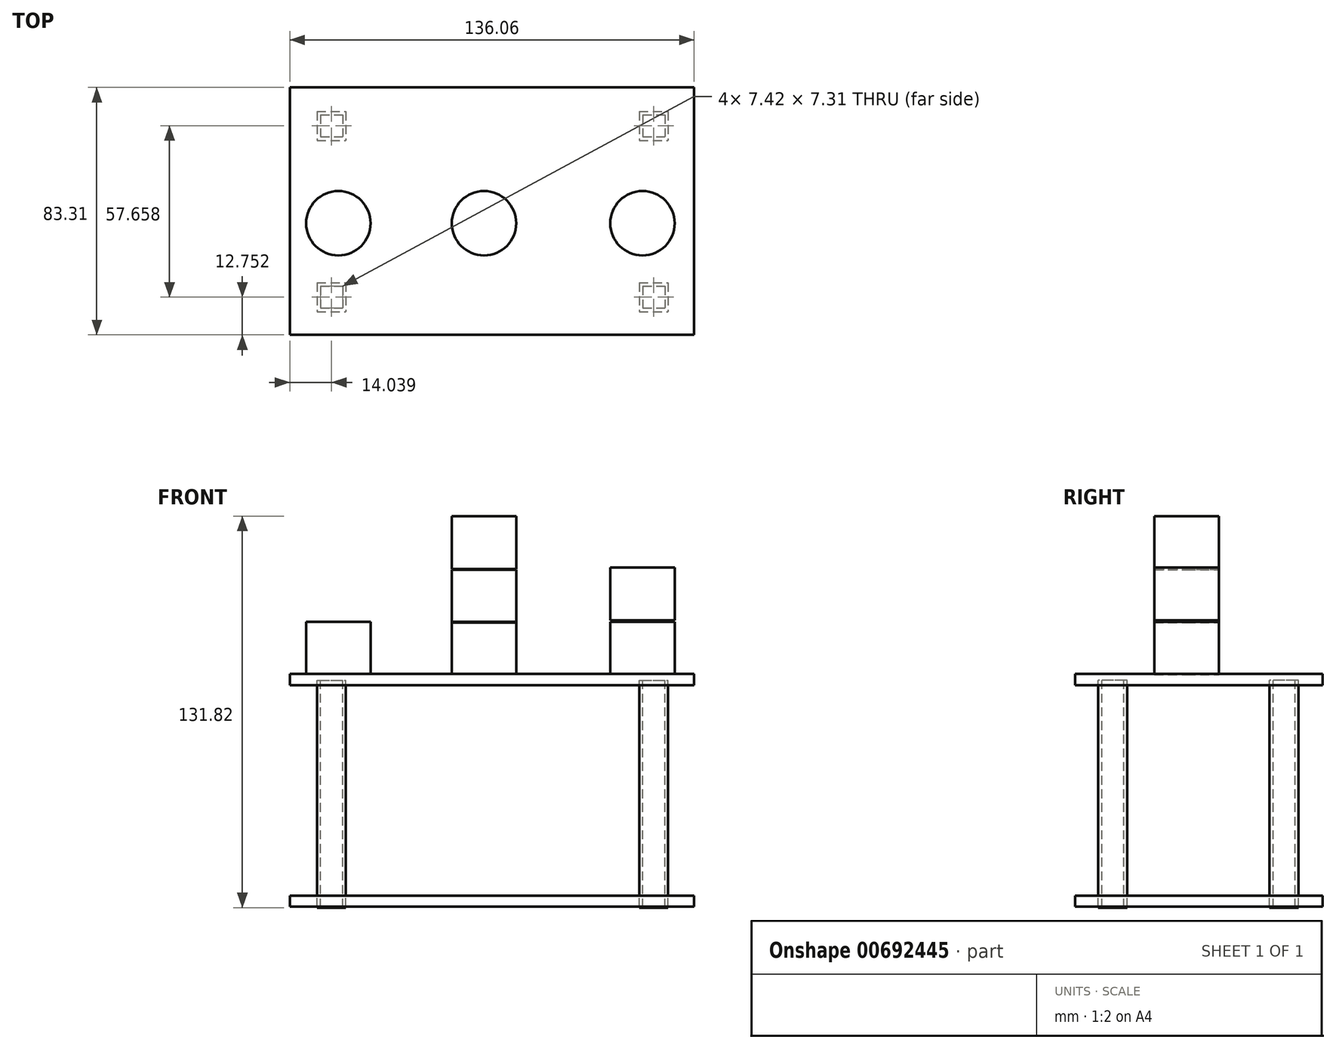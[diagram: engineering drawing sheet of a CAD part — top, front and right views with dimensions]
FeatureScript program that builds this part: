
annotation { "Feature Type Name" : "Feature", "Feature Type Description" : "" }
export const myFeature = defineFeature(function(context is Context, id is Id, definition is map)
    precondition{}
    {
        {
            var Q0;
            Q0=qCreatedBy(makeId("Front.planeOp"),FACE);
            var sketch = newSketch(context, id + "F0", { "sketchPlane" : qUnion([Q0])});
            skLineSegment(sketch, "E0", {"start": v(-67.33, -59.66) * mm, "end": v(68.73, -59.66) * mm});
            skLineSegment(sketch, "E1", {"start": v(68.73, -55.94) * mm, "end": v(-67.33, -55.94) * mm});
            skLineSegment(sketch, "E2", {"start": v(-67.33, -55.94) * mm, "end": v(-67.33, -59.66) * mm});
            skLineSegment(sketch, "E3", {"start": v(68.73, -55.94) * mm, "end": v(68.73, -59.66) * mm});
            skLineSegment(sketch, "E4", {"start": v(-67.33, 14.99) * mm, "end": v(68.73, 14.99) * mm});
            skLineSegment(sketch, "E5", {"start": v(68.73, 18.7) * mm, "end": v(-67.33, 18.7) * mm});
            skLineSegment(sketch, "E6", {"start": v(-67.33, 18.7) * mm, "end": v(-67.33, 14.99) * mm});
            skLineSegment(sketch, "E7", {"start": v(68.73, 18.7) * mm, "end": v(68.73, 14.99) * mm});
            skLineSegment(sketch, "E8", {"start": v(-56.17, 14.99) * mm, "end": v(-56.17, -55.94) * mm});
            skLineSegment(sketch, "E9", {"start": v(-52.45, 14.99) * mm, "end": v(-52.45, -55.94) * mm});
            skLineSegment(sketch, "E10", {"start": v(53.46, 15.34) * mm, "end": v(53.46, -55.58) * mm});
            skLineSegment(sketch, "E11", {"start": v(57.18, 15.34) * mm, "end": v(57.18, -55.58) * mm});
            skSolve(sketch);
        }
        {
            var Q0;
            Q0=makeQuery(id+"F0.imprint","IMPRINT",FACE,{"disambiguationData":[TD([[makeQuery(id+"F0.imprint","IMPRINT",EDGE,{"derivedFrom":sQuery(id+"F0.wireOp",EDGE,"E5")}),1.0]])]});
            var Q1;
            Q1=makeQuery(id+"F0.imprint","IMPRINT",FACE,{"disambiguationData":[TD([[makeQuery(id+"F0.imprint","IMPRINT",EDGE,{"derivedFrom":sQuery(id+"F0.wireOp",EDGE,"E0")}),1.0]])]});
            extrude(context, id + "F1", {"entities" : qUnion([Q0, Q1]), "depth" : 83.31 * mm, "offsetDistance" : 25.4 * mm});
        }
        {
            var Q0;
            Q0=makeQuery(id+"F1.opExtrude","SWEPT_FACE",FACE,{"disambiguationData":[OSD([sQuery(id+"F0.wireOp",EDGE,"E0")])]});
            var sketch = newSketch(context, id + "F2", { "sketchPlane" : qUnion([Q0])});
            skLineSegment(sketch, "E12.bottom", {"start": v(-58.2, 8.09) * mm, "end": v(-48.46, 8.09) * mm});
            skLineSegment(sketch, "E12.top", {"start": v(-58.2, 17.82) * mm, "end": v(-48.46, 17.82) * mm});
            skLineSegment(sketch, "E12.left", {"start": v(-58.2, 8.09) * mm, "end": v(-58.2, 17.82) * mm});
            skLineSegment(sketch, "E12.right", {"start": v(-48.46, 8.09) * mm, "end": v(-48.46, 17.82) * mm});
            skLineSegment(sketch, "E13.bottom", {"start": v(-57, 9.24) * mm, "end": v(-49.58, 9.24) * mm});
            skLineSegment(sketch, "E13.top", {"start": v(-57, 16.55) * mm, "end": v(-49.58, 16.55) * mm});
            skLineSegment(sketch, "E13.left", {"start": v(-57, 9.24) * mm, "end": v(-57, 16.55) * mm});
            skLineSegment(sketch, "E13.right", {"start": v(-49.58, 9.24) * mm, "end": v(-49.58, 16.55) * mm});
            skLineSegment(sketch, "E14.bottom", {"start": v(52.21, 8.09) * mm, "end": v(61.95, 8.09) * mm});
            skLineSegment(sketch, "E14.top", {"start": v(52.21, 17.82) * mm, "end": v(61.95, 17.82) * mm});
            skLineSegment(sketch, "E14.left", {"start": v(52.21, 8.09) * mm, "end": v(52.21, 17.82) * mm});
            skLineSegment(sketch, "E14.right", {"start": v(61.95, 8.09) * mm, "end": v(61.95, 17.82) * mm});
            skLineSegment(sketch, "E15.bottom", {"start": v(53.41, 9.24) * mm, "end": v(60.83, 9.24) * mm});
            skLineSegment(sketch, "E15.top", {"start": v(53.41, 16.55) * mm, "end": v(60.83, 16.55) * mm});
            skLineSegment(sketch, "E15.left", {"start": v(53.41, 9.24) * mm, "end": v(53.41, 16.55) * mm});
            skLineSegment(sketch, "E15.right", {"start": v(60.83, 9.24) * mm, "end": v(60.83, 16.55) * mm});
            skLineSegment(sketch, "E16.bottom", {"start": v(-58.2, 64.06) * mm, "end": v(-48.46, 64.06) * mm});
            skLineSegment(sketch, "E16.top", {"start": v(-58.2, 73.8) * mm, "end": v(-48.46, 73.8) * mm});
            skLineSegment(sketch, "E16.left", {"start": v(-58.2, 64.06) * mm, "end": v(-58.2, 73.8) * mm});
            skLineSegment(sketch, "E16.right", {"start": v(-48.46, 64.06) * mm, "end": v(-48.46, 73.8) * mm});
            skLineSegment(sketch, "E17.bottom", {"start": v(-57, 65.22) * mm, "end": v(-49.58, 65.22) * mm});
            skLineSegment(sketch, "E17.top", {"start": v(-57, 72.53) * mm, "end": v(-49.58, 72.53) * mm});
            skLineSegment(sketch, "E17.left", {"start": v(-57, 65.22) * mm, "end": v(-57, 72.53) * mm});
            skLineSegment(sketch, "E17.right", {"start": v(-49.58, 65.22) * mm, "end": v(-49.58, 72.53) * mm});
            skLineSegment(sketch, "E18.bottom", {"start": v(52.21, 64.06) * mm, "end": v(61.95, 64.06) * mm});
            skLineSegment(sketch, "E18.top", {"start": v(52.21, 73.8) * mm, "end": v(61.95, 73.8) * mm});
            skLineSegment(sketch, "E18.left", {"start": v(52.21, 64.06) * mm, "end": v(52.21, 73.8) * mm});
            skLineSegment(sketch, "E18.right", {"start": v(61.95, 64.06) * mm, "end": v(61.95, 73.8) * mm});
            skLineSegment(sketch, "E19.bottom", {"start": v(53.41, 65.22) * mm, "end": v(60.83, 65.22) * mm});
            skLineSegment(sketch, "E19.top", {"start": v(53.41, 72.53) * mm, "end": v(60.83, 72.53) * mm});
            skLineSegment(sketch, "E19.left", {"start": v(53.41, 65.22) * mm, "end": v(53.41, 72.53) * mm});
            skLineSegment(sketch, "E19.right", {"start": v(60.83, 65.22) * mm, "end": v(60.83, 72.53) * mm});
            skSolve(sketch);
        }
        {
            var Q0;
            Q0=makeQuery(id+"F2.imprint","IMPRINT",FACE,{"disambiguationData":[TD([[makeQuery(id+"F2.imprint","IMPRINT",EDGE,{"derivedFrom":sQuery(id+"F2.wireOp",EDGE,"E12.bottom")}),1.0]])]});
            extrude(context, id + "F3", {"entities" : qUnion([Q0]), "depth" : 0.28 * mm, "offsetDistance" : 25.4 * mm, "hasSecondDirection" : true, "secondDirectionOppositeDirection" : true, "secondDirectionDepth" : 76.2 * mm});
        }
        {
            var Q0;
            Q0=makeQuery(id+"F3.opExtrude","SWEPT_BODY",BODY,{"disambiguationData":[OSD([sQuery(id+"F2.wireOp",EDGE,"E12.bottom"),sQuery(id+"F2.wireOp",EDGE,"E12.top"),sQuery(id+"F2.wireOp",EDGE,"E12.left"),sQuery(id+"F2.wireOp",EDGE,"E12.right"),sQuery(id+"F2.wireOp",EDGE,"E13.bottom"),sQuery(id+"F2.wireOp",EDGE,"E13.top"),sQuery(id+"F2.wireOp",EDGE,"E13.left"),sQuery(id+"F2.wireOp",EDGE,"E13.right")])]});
            transform(context, id + "F4", {"entities" : qUnion([Q0]), "transformType" : TransformType.TRANSLATION_3D, "dx" : 108.46 * mm, "dy" : 0 * mm, "dz" : 0 * mm, "makeCopy" : true});
        }
        {
            var Q0;
            Q0=makeQuery(id+"F3.opExtrude","SWEPT_BODY",BODY,{"disambiguationData":[OSD([sQuery(id+"F2.wireOp",EDGE,"E12.bottom"),sQuery(id+"F2.wireOp",EDGE,"E12.top"),sQuery(id+"F2.wireOp",EDGE,"E12.left"),sQuery(id+"F2.wireOp",EDGE,"E12.right"),sQuery(id+"F2.wireOp",EDGE,"E13.bottom"),sQuery(id+"F2.wireOp",EDGE,"E13.top"),sQuery(id+"F2.wireOp",EDGE,"E13.left"),sQuery(id+"F2.wireOp",EDGE,"E13.right")])]});
            var Q1;
            Q1=makeQuery(id+"F4.opPattern","COPY",BODY,{"derivedFrom":makeQuery(id+"F3.opExtrude","SWEPT_BODY",BODY,{"disambiguationData":[OSD([sQuery(id+"F2.wireOp",EDGE,"E12.bottom"),sQuery(id+"F2.wireOp",EDGE,"E12.top"),sQuery(id+"F2.wireOp",EDGE,"E12.left"),sQuery(id+"F2.wireOp",EDGE,"E12.right"),sQuery(id+"F2.wireOp",EDGE,"E13.bottom"),sQuery(id+"F2.wireOp",EDGE,"E13.top"),sQuery(id+"F2.wireOp",EDGE,"E13.left"),sQuery(id+"F2.wireOp",EDGE,"E13.right")])]}),"instanceName":"1"});
            transform(context, id + "F5", {"entities" : qUnion([Q0, Q1]), "transformType" : TransformType.TRANSLATION_3D, "dx" : 0 * mm, "dy" : -57.66 * mm, "dz" : 0 * mm, "makeCopy" : true});
        }
        {
            var Q0;
            Q0=makeQuery(id+"F4.opPattern","COPY",BODY,{"derivedFrom":makeQuery(id+"F3.opExtrude","SWEPT_BODY",BODY,{"disambiguationData":[OSD([sQuery(id+"F2.wireOp",EDGE,"E12.bottom"),sQuery(id+"F2.wireOp",EDGE,"E12.top"),sQuery(id+"F2.wireOp",EDGE,"E12.left"),sQuery(id+"F2.wireOp",EDGE,"E12.right"),sQuery(id+"F2.wireOp",EDGE,"E13.bottom"),sQuery(id+"F2.wireOp",EDGE,"E13.top"),sQuery(id+"F2.wireOp",EDGE,"E13.left"),sQuery(id+"F2.wireOp",EDGE,"E13.right")])]}),"instanceName":"1"});
            var Q1;
            Q1=makeQuery(id+"F1.opExtrude","SWEPT_BODY",BODY,{"disambiguationData":[OSD([sQuery(id+"F0.wireOp",EDGE,"E0"),sQuery(id+"F0.wireOp",EDGE,"E1"),sQuery(id+"F0.wireOp",EDGE,"E2"),sQuery(id+"F0.wireOp",EDGE,"E3")])]});
            var Q2;
            Q2=makeQuery(id+"F1.opExtrude","SWEPT_BODY",BODY,{"disambiguationData":[OSD([sQuery(id+"F0.wireOp",EDGE,"E4"),sQuery(id+"F0.wireOp",EDGE,"E5"),sQuery(id+"F0.wireOp",EDGE,"E6"),sQuery(id+"F0.wireOp",EDGE,"E7")])]});
            var Q3;
            Q3=makeQuery(id+"F3.opExtrude","SWEPT_BODY",BODY,{"disambiguationData":[OSD([sQuery(id+"F2.wireOp",EDGE,"E12.bottom"),sQuery(id+"F2.wireOp",EDGE,"E12.top"),sQuery(id+"F2.wireOp",EDGE,"E12.left"),sQuery(id+"F2.wireOp",EDGE,"E12.right"),sQuery(id+"F2.wireOp",EDGE,"E13.bottom"),sQuery(id+"F2.wireOp",EDGE,"E13.top"),sQuery(id+"F2.wireOp",EDGE,"E13.left"),sQuery(id+"F2.wireOp",EDGE,"E13.right")])]});
            var Q4;
            Q4=makeQuery(id+"F5.opPattern","COPY",BODY,{"derivedFrom":makeQuery(id+"F3.opExtrude","SWEPT_BODY",BODY,{"disambiguationData":[OSD([sQuery(id+"F2.wireOp",EDGE,"E12.bottom"),sQuery(id+"F2.wireOp",EDGE,"E12.top"),sQuery(id+"F2.wireOp",EDGE,"E12.left"),sQuery(id+"F2.wireOp",EDGE,"E12.right"),sQuery(id+"F2.wireOp",EDGE,"E13.bottom"),sQuery(id+"F2.wireOp",EDGE,"E13.top"),sQuery(id+"F2.wireOp",EDGE,"E13.left"),sQuery(id+"F2.wireOp",EDGE,"E13.right")])]}),"instanceName":"1"});
            var Q5;
            Q5=makeQuery(id+"F5.opPattern","COPY",BODY,{"derivedFrom":makeQuery(id+"F4.opPattern","COPY",BODY,{"derivedFrom":makeQuery(id+"F3.opExtrude","SWEPT_BODY",BODY,{"disambiguationData":[OSD([sQuery(id+"F2.wireOp",EDGE,"E12.bottom"),sQuery(id+"F2.wireOp",EDGE,"E12.top"),sQuery(id+"F2.wireOp",EDGE,"E12.left"),sQuery(id+"F2.wireOp",EDGE,"E12.right"),sQuery(id+"F2.wireOp",EDGE,"E13.bottom"),sQuery(id+"F2.wireOp",EDGE,"E13.top"),sQuery(id+"F2.wireOp",EDGE,"E13.left"),sQuery(id+"F2.wireOp",EDGE,"E13.right")])]}),"instanceName":"1"}),"instanceName":"1"});
            transform(context, id + "F6", {"entities" : qUnion([Q0, Q1, Q2, Q3, Q4, Q5]), "transformType" : TransformType.TRANSLATION_3D, "dx" : 285.75 * mm, "dy" : 0 * mm, "dz" : 0 * mm, "makeCopy" : false});
        }
        {
            var Q0;
            Q0=qCreatedBy(makeId("Top.planeOp"),FACE);
            var sketch = newSketch(context, id + "F7", { "sketchPlane" : qUnion([Q0])});
            skCircle(sketch, "E20", {"center": v(-23.07, 19.55) * mm, "radius": 10.84 * mm});
            skSolve(sketch);
        }
        {
            var Q0;
            Q0=makeQuery(id+"F7.imprint","IMPRINT",FACE,{"disambiguationData":[TD([[makeQuery(id+"F7.imprint","IMPRINT",EDGE,{"derivedFrom":sQuery(id+"F7.wireOp",EDGE,"E20")}),1.0]])]});
            extrude(context, id + "F8", {"entities" : qUnion([Q0]), "depth" : 17.78 * mm, "offsetDistance" : 25.4 * mm});
        }
        {
            var Q0;
            Q0=makeQuery(id+"F8.opExtrude","SWEPT_BODY",BODY,{"disambiguationData":[OSD([sQuery(id+"F7.wireOp",EDGE,"E20")])]});
            transform(context, id + "F9", {"entities" : qUnion([Q0]), "transformType" : TransformType.TRANSLATION_3D, "dx" : 49.02 * mm, "dy" : 0 * mm, "dz" : 0 * mm, "makeCopy" : true});
        }
        {
            var Q0;
            Q0=makeQuery(id+"F8.opExtrude","SWEPT_BODY",BODY,{"disambiguationData":[OSD([sQuery(id+"F7.wireOp",EDGE,"E20")])]});
            var Q1;
            Q1=makeQuery(id+"F9.opPattern","COPY",BODY,{"derivedFrom":makeQuery(id+"F8.opExtrude","SWEPT_BODY",BODY,{"disambiguationData":[OSD([sQuery(id+"F7.wireOp",EDGE,"E20")])]}),"instanceName":"1"});
            transform(context, id + "F10", {"entities" : qUnion([Q0, Q1]), "transformType" : TransformType.TRANSLATION_3D, "dx" : -24.9 * mm, "dy" : 0 * mm, "dz" : 0 * mm, "makeCopy" : false});
        }
        {
            var Q0;
            Q0=makeQuery(id+"F8.opExtrude","SWEPT_BODY",BODY,{"disambiguationData":[OSD([sQuery(id+"F7.wireOp",EDGE,"E20")])]});
            transform(context, id + "F11", {"entities" : qUnion([Q0]), "transformType" : TransformType.TRANSLATION_3D, "dx" : 102.36 * mm, "dy" : 0 * mm, "dz" : 0 * mm, "makeCopy" : true});
        }
        {
            var Q0;
            Q0=makeQuery(id+"F9.opPattern","COPY",BODY,{"derivedFrom":makeQuery(id+"F8.opExtrude","SWEPT_BODY",BODY,{"disambiguationData":[OSD([sQuery(id+"F7.wireOp",EDGE,"E20")])]}),"instanceName":"1"});
            transform(context, id + "F12", {"entities" : qUnion([Q0]), "transformType" : TransformType.TRANSLATION_3D, "dx" : 0 * mm, "dy" : 0 * mm, "dz" : 17.53 * mm, "makeCopy" : true});
        }
        {
            var Q0;
            Q0=makeQuery(id+"F9.opPattern","COPY",BODY,{"derivedFrom":makeQuery(id+"F8.opExtrude","SWEPT_BODY",BODY,{"disambiguationData":[OSD([sQuery(id+"F7.wireOp",EDGE,"E20")])]}),"instanceName":"1"});
            transform(context, id + "F13", {"entities" : qUnion([Q0]), "transformType" : TransformType.TRANSLATION_3D, "dx" : 0 * mm, "dy" : 0 * mm, "dz" : 35.56 * mm, "makeCopy" : true});
        }
        {
            var Q0;
            Q0=makeQuery(id+"F11.opPattern","COPY",BODY,{"derivedFrom":makeQuery(id+"F8.opExtrude","SWEPT_BODY",BODY,{"disambiguationData":[OSD([sQuery(id+"F7.wireOp",EDGE,"E20")])]}),"instanceName":"1"});
            transform(context, id + "F14", {"entities" : qUnion([Q0]), "transformType" : TransformType.TRANSLATION_3D, "dx" : 0 * mm, "dy" : 0 * mm, "dz" : 18.29 * mm, "makeCopy" : true});
        }
        {
            var Q0;
            Q0=makeQuery(id+"F8.opExtrude","SWEPT_BODY",BODY,{"disambiguationData":[OSD([sQuery(id+"F7.wireOp",EDGE,"E20")])]});
            var Q1;
            Q1=makeQuery(id+"F9.opPattern","COPY",BODY,{"derivedFrom":makeQuery(id+"F8.opExtrude","SWEPT_BODY",BODY,{"disambiguationData":[OSD([sQuery(id+"F7.wireOp",EDGE,"E20")])]}),"instanceName":"1"});
            var Q2;
            Q2=makeQuery(id+"F11.opPattern","COPY",BODY,{"derivedFrom":makeQuery(id+"F8.opExtrude","SWEPT_BODY",BODY,{"disambiguationData":[OSD([sQuery(id+"F7.wireOp",EDGE,"E20")])]}),"instanceName":"1"});
            var Q3;
            Q3=makeQuery(id+"F12.opPattern","COPY",BODY,{"derivedFrom":makeQuery(id+"F9.opPattern","COPY",BODY,{"derivedFrom":makeQuery(id+"F8.opExtrude","SWEPT_BODY",BODY,{"disambiguationData":[OSD([sQuery(id+"F7.wireOp",EDGE,"E20")])]}),"instanceName":"1"}),"instanceName":"1"});
            var Q4;
            Q4=makeQuery(id+"F14.opPattern","COPY",BODY,{"derivedFrom":makeQuery(id+"F11.opPattern","COPY",BODY,{"derivedFrom":makeQuery(id+"F8.opExtrude","SWEPT_BODY",BODY,{"disambiguationData":[OSD([sQuery(id+"F7.wireOp",EDGE,"E20")])]}),"instanceName":"1"}),"instanceName":"1"});
            var Q5;
            Q5=makeQuery(id+"F13.opPattern","COPY",BODY,{"derivedFrom":makeQuery(id+"F9.opPattern","COPY",BODY,{"derivedFrom":makeQuery(id+"F8.opExtrude","SWEPT_BODY",BODY,{"disambiguationData":[OSD([sQuery(id+"F7.wireOp",EDGE,"E20")])]}),"instanceName":"1"}),"instanceName":"1"});
            transform(context, id + "F15", {"entities" : qUnion([Q0, Q1, Q2, Q3, Q4, Q5]), "transformType" : TransformType.TRANSLATION_3D, "dx" : 282.7 * mm, "dy" : -65.28 * mm, "dz" : 18.54 * mm, "makeCopy" : false});
        }
    });
